# Revit family: 206_HDE-CO-_-_
name_source: partatom
category: Duct Accessories
units: mm (PartAtom-declared; Revit-internal decimal feet)

## family parameters
Always vertical = Yes
Cut with Voids When Loaded = No
Part Type = Breaks Into
Round Connector Dimension = Use Diameter
Shared = No
Work Plane-Based = No

## types (24) — shared parameters
CAT0 = Yes
Description = ELECTRIC ROUND DUCT HEATERS
Manufacturer = Alnor
QmdConnectorList = 201;D;202;D
URL = http://www.ventilation-alnor.co.uk
magiPartTypeId = 206
magiProductFamilyId = HDE-CO-*-*

## per-type parameters (varying)
| type | A | A2 | B2 | D | DH | H2D | L | L2D | LL | R | RH | W2D | Z1 |
| HDE-CO-100-0.3 | 280 mm  [stored 0.918635 ft] | 140 mm  [stored 0.459318 ft] | 48 mm  [stored 0.15748 ft] | 100 mm | 110 mm  [stored 0.360892 ft] | 100 mm  [stored 0.328084 ft] | 380 mm  [stored 1.24672 ft] | 380 mm  [stored 1.24672 ft] | 190 mm  [stored 0.62336 ft] | 50 mm  [stored 0.164042 ft] | 36 mm | 100 mm  [stored 0.328084 ft] | 14 mm  [stored 0.0459318 ft] |
| HDE-CO-250-2.0 | 300 mm | 150 mm | 95 mm  [stored 0.31168 ft] | 250 mm | 185 mm | 250 mm | 400 mm | 400 mm | 200 mm | 125 mm | 44 mm | 250 mm | 81 mm |
| HDE-CO-250-1.5 | 300 mm | 150 mm | 95 mm  [stored 0.31168 ft] | 250 mm | 185 mm | 250 mm | 400 mm | 400 mm | 200 mm | 125 mm | 44 mm | 250 mm | 81 mm |
| HDE-CO-250-1.0 | 300 mm | 150 mm | 95 mm  [stored 0.31168 ft] | 250 mm | 185 mm | 250 mm | 400 mm | 400 mm | 200 mm | 125 mm | 44 mm | 250 mm | 81 mm |
| HDE-CO-250-0.5 | 300 mm | 150 mm | 95 mm  [stored 0.31168 ft] | 250 mm | 185 mm | 250 mm | 400 mm | 400 mm | 200 mm | 125 mm | 44 mm | 250 mm | 81 mm |
| HDE-CO-200-2.0 | 300 mm | 150 mm | 80 mm | 200 mm | 160 mm | 200 mm | 400 mm | 400 mm | 200 mm | 100 mm  [stored 0.328084 ft] | 40 mm | 200 mm | 60 mm |
| HDE-CO-200-1.5 | 300 mm | 150 mm | 80 mm | 200 mm | 160 mm | 200 mm | 400 mm | 400 mm | 200 mm | 100 mm  [stored 0.328084 ft] | 40 mm | 200 mm | 60 mm |
| HDE-CO-200-1.0 | 300 mm | 150 mm | 80 mm | 200 mm | 160 mm | 200 mm | 400 mm | 400 mm | 200 mm | 100 mm  [stored 0.328084 ft] | 40 mm | 200 mm | 60 mm |
| HDE-CO-200-0.5 | 300 mm | 150 mm | 80 mm | 200 mm | 160 mm | 200 mm | 400 mm | 400 mm | 200 mm | 100 mm  [stored 0.328084 ft] | 40 mm | 200 mm | 60 mm |
| HDE-CO-160-2.0 | 280 mm  [stored 0.918635 ft] | 140 mm  [stored 0.459318 ft] | 60 mm | 160 mm | 140 mm  [stored 0.459318 ft] | 160 mm | 380 mm  [stored 1.24672 ft] | 380 mm  [stored 1.24672 ft] | 190 mm  [stored 0.62336 ft] | 80 mm | 27 mm | 160 mm | 53 mm |
| HDE-CO-160-1.5 | 280 mm  [stored 0.918635 ft] | 140 mm  [stored 0.459318 ft] | 60 mm | 160 mm | 140 mm  [stored 0.459318 ft] | 160 mm | 380 mm  [stored 1.24672 ft] | 380 mm  [stored 1.24672 ft] | 190 mm  [stored 0.62336 ft] | 80 mm | 27 mm | 160 mm | 53 mm |
| HDE-CO-160-1.0 | 280 mm  [stored 0.918635 ft] | 140 mm  [stored 0.459318 ft] | 60 mm | 160 mm | 140 mm  [stored 0.459318 ft] | 160 mm | 380 mm  [stored 1.24672 ft] | 380 mm  [stored 1.24672 ft] | 190 mm  [stored 0.62336 ft] | 80 mm | 27 mm | 160 mm | 53 mm |
| HDE-CO-160-0.5 | 280 mm  [stored 0.918635 ft] | 140 mm  [stored 0.459318 ft] | 60 mm | 160 mm | 140 mm  [stored 0.459318 ft] | 160 mm | 380 mm  [stored 1.24672 ft] | 380 mm  [stored 1.24672 ft] | 190 mm  [stored 0.62336 ft] | 80 mm | 27 mm | 160 mm | 53 mm |
| HDE-CO-150-2.0 | 280 mm  [stored 0.918635 ft] | 140 mm  [stored 0.459318 ft] | 60 mm | 150 mm | 135 mm | 150 mm | 380 mm  [stored 1.24672 ft] | 380 mm  [stored 1.24672 ft] | 190 mm  [stored 0.62336 ft] | 75 mm | 30 mm  [stored 0.0984252 ft] | 150 mm | 45 mm |
| HDE-CO-150-1.5 | 280 mm  [stored 0.918635 ft] | 140 mm  [stored 0.459318 ft] | 60 mm | 150 mm | 135 mm | 150 mm | 380 mm  [stored 1.24672 ft] | 380 mm  [stored 1.24672 ft] | 190 mm  [stored 0.62336 ft] | 75 mm | 30 mm  [stored 0.0984252 ft] | 150 mm | 45 mm |
| HDE-CO-150-1.0 | 280 mm  [stored 0.918635 ft] | 140 mm  [stored 0.459318 ft] | 60 mm | 150 mm | 135 mm | 150 mm | 380 mm  [stored 1.24672 ft] | 380 mm  [stored 1.24672 ft] | 190 mm  [stored 0.62336 ft] | 75 mm | 30 mm  [stored 0.0984252 ft] | 150 mm | 45 mm |
| HDE-CO-150-0.5 | 280 mm  [stored 0.918635 ft] | 140 mm  [stored 0.459318 ft] | 60 mm | 150 mm | 135 mm | 150 mm | 380 mm  [stored 1.24672 ft] | 380 mm  [stored 1.24672 ft] | 190 mm  [stored 0.62336 ft] | 75 mm | 30 mm  [stored 0.0984252 ft] | 150 mm | 45 mm |
| HDE-CO-125-1.5 | 280 mm  [stored 0.918635 ft] | 140 mm  [stored 0.459318 ft] | 50 mm  [stored 0.164042 ft] | 125 mm | 123 mm | 125 mm | 380 mm  [stored 1.24672 ft] | 380 mm  [stored 1.24672 ft] | 190 mm  [stored 0.62336 ft] | 63 mm | 25 mm  [stored 0.082021 ft] | 125 mm | 38 mm |
| HDE-CO-125-1.2 | 280 mm  [stored 0.918635 ft] | 140 mm  [stored 0.459318 ft] | 50 mm  [stored 0.164042 ft] | 125 mm | 123 mm | 125 mm | 380 mm  [stored 1.24672 ft] | 380 mm  [stored 1.24672 ft] | 190 mm  [stored 0.62336 ft] | 63 mm | 25 mm  [stored 0.082021 ft] | 125 mm | 38 mm |
| HDE-CO-125-0.9 | 280 mm  [stored 0.918635 ft] | 140 mm  [stored 0.459318 ft] | 50 mm  [stored 0.164042 ft] | 125 mm | 123 mm | 125 mm | 380 mm  [stored 1.24672 ft] | 380 mm  [stored 1.24672 ft] | 190 mm  [stored 0.62336 ft] | 63 mm | 25 mm  [stored 0.082021 ft] | 125 mm | 38 mm |
| HDE-CO-125-0.6 | 280 mm  [stored 0.918635 ft] | 140 mm  [stored 0.459318 ft] | 50 mm  [stored 0.164042 ft] | 125 mm | 123 mm | 125 mm | 380 mm  [stored 1.24672 ft] | 380 mm  [stored 1.24672 ft] | 190 mm  [stored 0.62336 ft] | 63 mm | 25 mm  [stored 0.082021 ft] | 125 mm | 38 mm |
| HDE-CO-100-1.2 | 280 mm  [stored 0.918635 ft] | 140 mm  [stored 0.459318 ft] | 48 mm  [stored 0.15748 ft] | 100 mm | 110 mm  [stored 0.360892 ft] | 100 mm  [stored 0.328084 ft] | 380 mm  [stored 1.24672 ft] | 380 mm  [stored 1.24672 ft] | 190 mm  [stored 0.62336 ft] | 50 mm  [stored 0.164042 ft] | 36 mm | 100 mm  [stored 0.328084 ft] | 14 mm  [stored 0.0459318 ft] |
| HDE-CO-100-0.9 | 280 mm  [stored 0.918635 ft] | 140 mm  [stored 0.459318 ft] | 48 mm  [stored 0.15748 ft] | 100 mm | 110 mm  [stored 0.360892 ft] | 100 mm  [stored 0.328084 ft] | 380 mm  [stored 1.24672 ft] | 380 mm  [stored 1.24672 ft] | 190 mm  [stored 0.62336 ft] | 50 mm  [stored 0.164042 ft] | 36 mm | 100 mm  [stored 0.328084 ft] | 14 mm  [stored 0.0459318 ft] |
| HDE-CO-100-0.6 | 280 mm  [stored 0.918635 ft] | 140 mm  [stored 0.459318 ft] | 48 mm  [stored 0.15748 ft] | 100 mm | 110 mm  [stored 0.360892 ft] | 100 mm  [stored 0.328084 ft] | 380 mm  [stored 1.24672 ft] | 380 mm  [stored 1.24672 ft] | 190 mm  [stored 0.62336 ft] | 50 mm  [stored 0.164042 ft] | 36 mm | 100 mm  [stored 0.328084 ft] | 14 mm  [stored 0.0459318 ft] |

note: column(s) folded — value = type name in every type: MC Product Code, magiProductId

note: [stored X ft] marks values corroborated as IEEE doubles in the binary element streams (Revit-internal decimal feet)

## geometry (parser evidence)
native form markers: Blend x4, Sweep x1
no freeform markers — native parametric forms only
